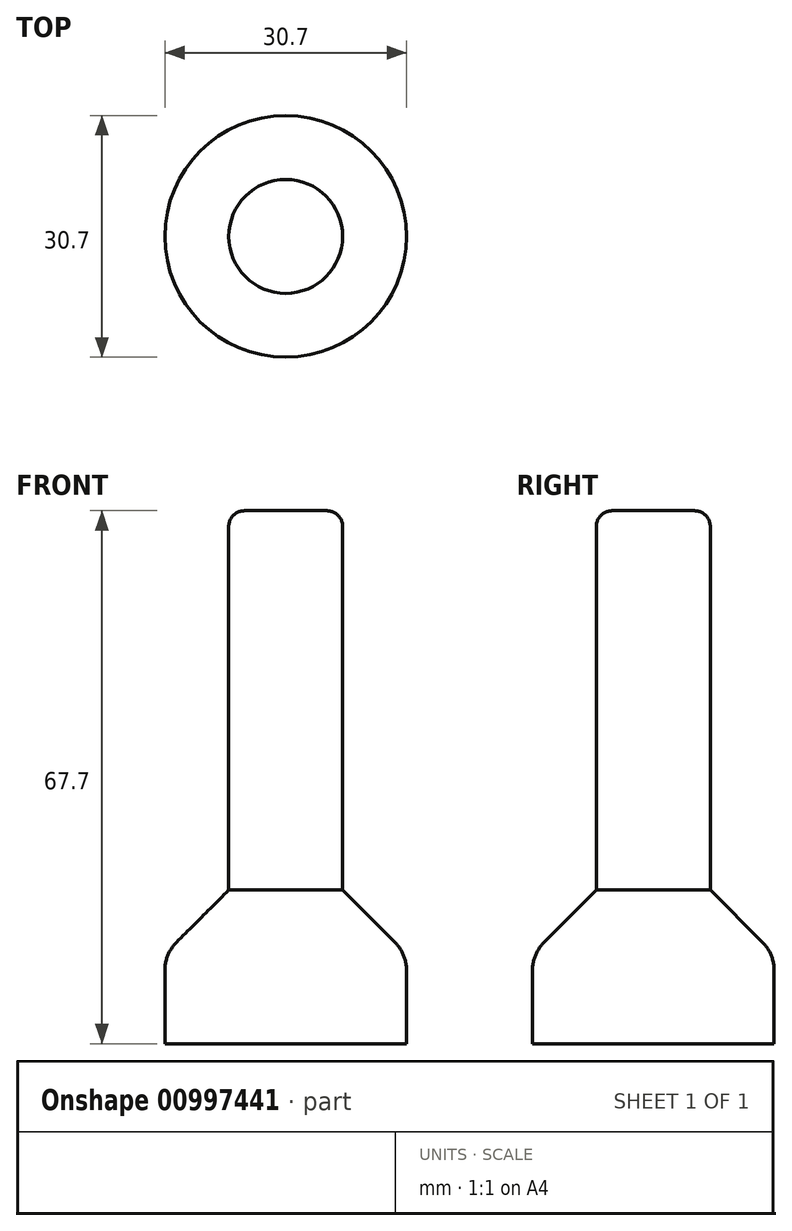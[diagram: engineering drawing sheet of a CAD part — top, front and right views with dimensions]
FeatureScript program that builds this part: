
annotation { "Feature Type Name" : "Feature", "Feature Type Description" : "" }
export const myFeature = defineFeature(function(context is Context, id is Id, definition is map)
    precondition{}
    {
        {
            var Q0;
            Q0=qCreatedBy(makeId("Top.planeOp"),FACE);
            var sketch = newSketch(context, id + "F0", { "sketchPlane" : qUnion([Q0])});
            skCircle(sketch, "E0", {"center": v(0, 0) * mm, "radius": 7.23 * mm});
            skSolve(sketch);
        }
        {
            var Q0;
            Q0 = qSketchRegion(id + "F0", true);
            extrude(context, id + "F1", {"entities" : qUnion([Q0]), "depth" : 67.7 * mm, "offsetDistance" : 25 * mm});
        }
        {
            var Q0;
            Q0=qCreatedBy(makeId("Top.planeOp"),FACE);
            var sketch = newSketch(context, id + "F2", { "sketchPlane" : qUnion([Q0])});
            skCircle(sketch, "E1", {"center": v(0, 0) * mm, "radius": 15.35 * mm});
            skSolve(sketch);
        }
        {
            var Q0;
            Q0 = qSketchRegion(id + "F2", true);
            extrude(context, id + "F3", {"entities" : qUnion([Q0]), "operationType" : NewBodyOperationType.ADD, "depth" : 21.4 * mm, "offsetDistance" : 25 * mm});
        }
        {
            var Q0;
            Q0=makeQuery(id+"F1.opExtrude","CAP_EDGE",EDGE,{"disambiguationData":[OSD([sQuery(id+"F0.wireOp",EDGE,"E0")])],"isStart":false});
            fillet(context, id + "F4", {"entities" : qUnion([Q0]), "radius" : 2 * mm, "tangentPropagation" : true, "allowEdgeOverflow" : false});
        }
        {
            var Q0;
            Q0=makeQuery(id+"F3.opExtrude","CAP_EDGE",EDGE,{"disambiguationData":[OSD([sQuery(id+"F2.wireOp",EDGE,"E1")])],"isStart":false});
            chamfer(context, id + "F5", {"entities" : qUnion([Q0]), "width" : 10 * mm, "tangentPropagation" : true});
        }
        {
            var Q0;
            {var subQ0=sQuery(id+"F2.wireOp",EDGE,"E1");Q0=makeQuery(id+"F5.opChamfer","BLEND_EDGE",EDGE,{"blendedFrom":[makeQuery(id+"F3.opExtrude","CAP_EDGE",EDGE,{"disambiguationData":[OSD([subQ0])],"isStart":false}),makeQuery(id+"F3.opExtrude","SWEPT_FACE",FACE,{"disambiguationData":[OSD([subQ0])]})],"blendedInto":[makeQuery(id+"F3.opExtrude","SWEPT_FACE",FACE,{"disambiguationData":[OSD([subQ0])]})]});}
            fillet(context, id + "F6", {"entities" : qUnion([Q0]), "radius" : 5 * mm, "tangentPropagation" : true, "allowEdgeOverflow" : false});
        }
    });
